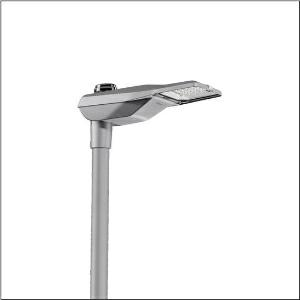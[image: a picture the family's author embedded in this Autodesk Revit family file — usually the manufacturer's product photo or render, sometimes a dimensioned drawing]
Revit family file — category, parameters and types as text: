
# Revit family: streetlight_sl_21_micro___stw1_0a_5xe5e37n08cb_b20b
name_source: partatom
category: Lighting Fixtures
units: mm (PartAtom-declared; Revit-internal decimal feet)

## family parameters
Cut with Voids When Loaded = No
Host = Face
Light Source = No
Part Type = Normal
Room Calculation Point = No
Round Connector Dimension = Use Diameter
Shared = No

## types (1)
- --- (1 x LED, 2290 lm, 15.8 W, 3000K)
    Apparent Load = 16 VA
    CIE Flux Codes = 38 75 98 100 100
    Color Rendering = 70
    Color Temperature = 3000K
    Default Elevation = 1800 mm
    Description = Streetlight SL 21 micro, mast luminaire, primary light control with lens, of PMMA, primary optical cover: cover, of toughened safety glass, transparent, light distribution: STW1.0a, light emission: direct distribution, primary light characteristic: asymmetric, installation type: post-top, LED, 3G 1.5mm², High Power LED, rated luminous flux: 2.290lm, luminous efficacy: 145lm/W, light colour: 730, colour temperature: 3000K, control: overheat protection, presetting dimming linear, constant luminous flux control, time-dependent luminous flux control, flexible luminous flux parameterisation, mains connection: 230..240V, AC, 50/60Hz, connection cable pre-assembled, cable length: 6,5m, wiring characteristics: H07RN-F, start of lifetime: 16W, end of service life: 16W, reduction: 8W, luminaire housing, of diecast aluminium (EN AC-44300), powder-coated, Siteco® metallic grey (DB 702S), corrosivity category C5 mid according to DIN EN ISO 12944, multi-level sealing system, sealing non-destructively replaceable, inclination adjustable: 0°, 5°, 10°, 15°, length: 528mm, width: 235mm, height: 110mm, spigot size: 76/60mm (post-top), protection rating (complete): IP66, insulation class (complete): insulation class I (protective earthing), certification: CE, ENEC, ENEC+, VDE, impact resistance: IK09, permissible operating ambient temperature for outdoor applications: -40..+50°C, standard-compliant lighting for roads and squares, packaging unit: 1 piece

Light Distribution: STW1.0a
    Height = 110 mm
    Lamp = 1 x LED
    Lamp Light Flux = 2290 lm
    Lamp Power = 15.8 W
    Lamp count = 1
    Length = 528 mm
    Luminous efficacy = 145 lm/W
    Manufacturer = Siteco
    ModVariant = No
    Model = 5XE5E37N08CB
    Number of Poles = 1
    OnlyDefault = Yes
    Power Factor = 1
    Product Name = Streetlight SL 21 micro | STW1.0a
    Product group = mast luminaire | pylon top
    ProductGroupID = 6100
    Protection Class = Protection class I
    Protection Degree = IP 66
    RLX_Detail_Level = 1
    RLX_Emergency_Light_Flux = 0 lm
    RLX_Emergency_Type = 0
    RLX_Emergency_Type_DB = No
    RlxData = <blob elided: 98921 chars, md5=0d3c824d>
    Socket = socket
    Standby Power = 0 W
    System Light Flux = 2290 lm
    System Power = 16 W
    Type Comments = factory setting: luminous flux: 100 % | dim-lin: 254 | 300 mA
    Type Image = l_1294375.jpg
    URL = http://relux.com
    VarID = @adj_085239
    Voltage = 0 V
    Weight = 0.00 kg
    Width = 235 mm

## geometry (parser evidence)
native form markers: Blend x4, Sweep x10
no freeform markers — native parametric forms only
